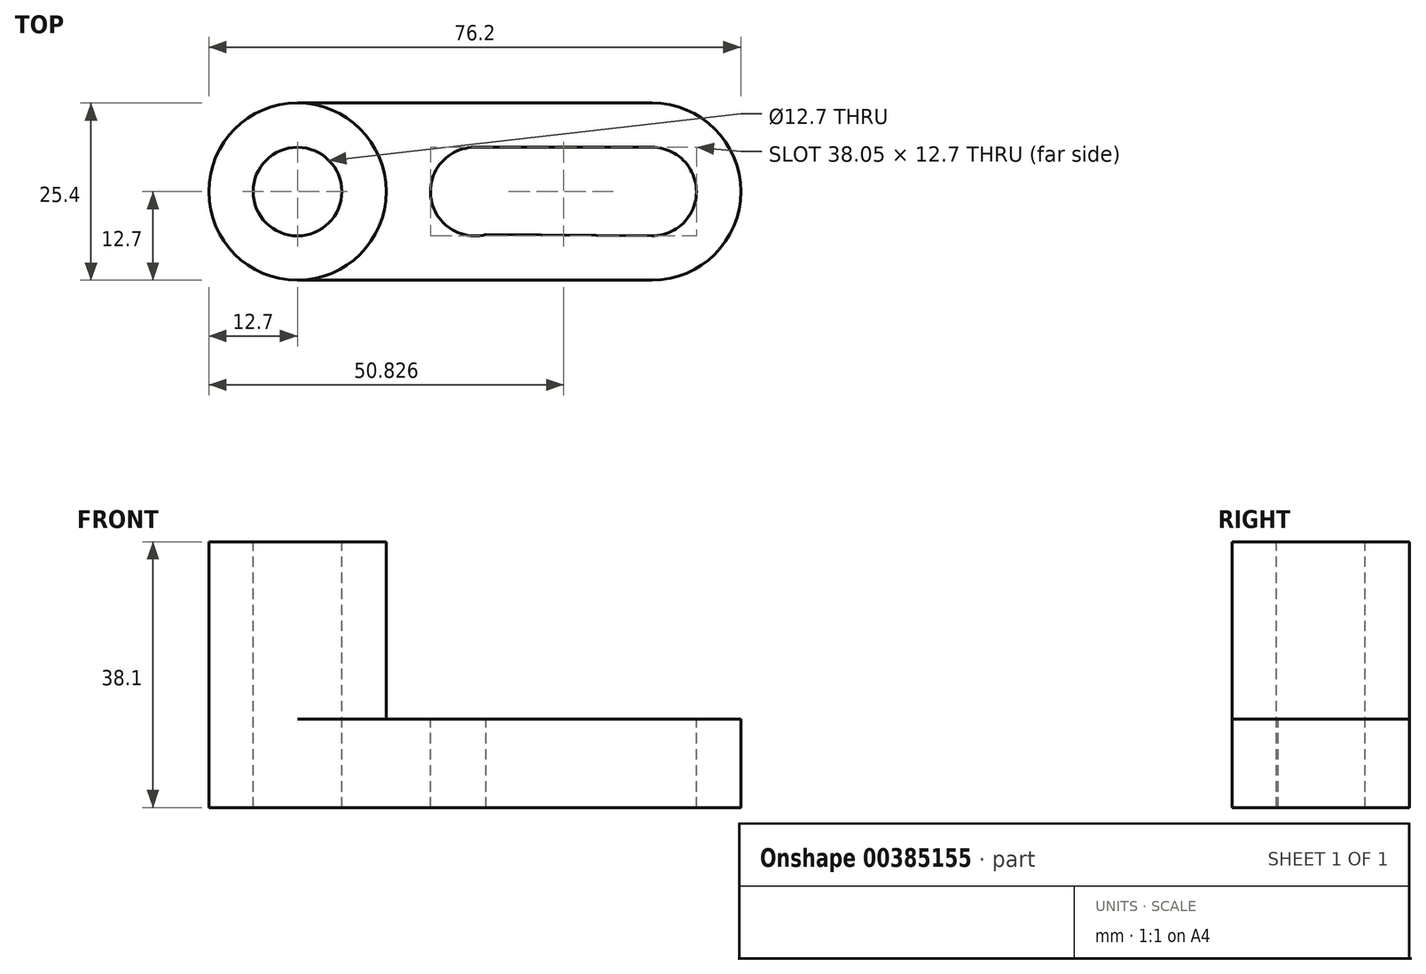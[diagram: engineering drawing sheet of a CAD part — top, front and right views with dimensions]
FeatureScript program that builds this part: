
annotation { "Feature Type Name" : "Feature", "Feature Type Description" : "" }
export const myFeature = defineFeature(function(context is Context, id is Id, definition is map)
    precondition{}
    {
        {
            var Q0;
            Q0=qCreatedBy(makeId("Front.planeOp"),FACE);
            var sketch = newSketch(context, id + "F0", { "sketchPlane" : qUnion([Q0])});
            skLineSegment(sketch, "E0", {"start": v(0, 0) * mm, "end": v(0, 38.1) * mm});
            skLineSegment(sketch, "E1", {"start": v(0, 38.1) * mm, "end": v(25.4, 38.1) * mm});
            skLineSegment(sketch, "E2", {"start": v(25.4, 38.1) * mm, "end": v(25.4, 12.7) * mm});
            skLineSegment(sketch, "E3", {"start": v(25.4, 12.7) * mm, "end": v(76.2, 12.7) * mm});
            skLineSegment(sketch, "E4", {"start": v(76.2, 12.7) * mm, "end": v(76.2, 0) * mm});
            skLineSegment(sketch, "E5", {"start": v(76.2, 0) * mm, "end": v(0, 0) * mm});
            skSolve(sketch);
        }
        {
            var Q0;
            Q0 = qSketchRegion(id + "F0", true);
            extrude(context, id + "F1", {"entities" : qUnion([Q0]), "depth" : 25.4 * mm});
        }
        {
            var Q0;
            Q0=makeQuery(id+"F1.opExtrude","SWEPT_FACE",FACE,{"disambiguationData":[OSD([sQuery(id+"F0.wireOp",EDGE,"E3")])]});
            var sketch = newSketch(context, id + "F2", { "sketchPlane" : qUnion([Q0])});
            skCircle(sketch, "E6", {"center": v(38.1, -12.7) * mm, "radius": 6.35 * mm});
            skCircle(sketch, "E7", {"center": v(63.5, -12.7) * mm, "radius": 6.35 * mm});
            skLineSegment(sketch, "E8", {"start": v(38.1, -6.35) * mm, "end": v(63.5, -6.35) * mm});
            skLineSegment(sketch, "E9", {"start": v(39.7, -18.84) * mm, "end": v(63.44, -19.05) * mm});
            skSolve(sketch);
        }
        {
            var Q0;
            {var subQ0=sQuery(id+"F2.wireOp",EDGE,"E6");var subQ1=makeQuery(id+"F2.imprint","INTERSECT",VERTEX,{"derivedFrom":[subQ0,sQuery(id+"F2.wireOp",EDGE,"E8")]});Q0=makeQuery(id+"F2.imprint","IMPRINT",FACE,{"disambiguationData":[TD([[makeQuery(id+"F2.imprint","IMPRINT",EDGE,{"disambiguationData":[TD([[subQ1,-1.0]])],"derivedFrom":subQ0}),1.0]])]});}
            var Q1;
            {var subQ0=sQuery(id+"F2.wireOp",EDGE,"E8");Q1=makeQuery(id+"F2.imprint","IMPRINT",FACE,{"disambiguationData":[TD([[makeQuery(id+"F2.imprint","IMPRINT",EDGE,{"derivedFrom":subQ0}),-1.0]])]});}
            var Q2;
            {var subQ0=sQuery(id+"F2.wireOp",EDGE,"E7");var subQ1=makeQuery(id+"F2.imprint","INTERSECT",VERTEX,{"derivedFrom":[subQ0,sQuery(id+"F2.wireOp",EDGE,"E8")]});Q2=makeQuery(id+"F2.imprint","IMPRINT",FACE,{"disambiguationData":[TD([[makeQuery(id+"F2.imprint","IMPRINT",EDGE,{"disambiguationData":[TD([[subQ1,-1.0]])],"derivedFrom":subQ0}),1.0]])]});}
            extrude(context, id + "F3", {"entities" : qUnion([Q0, Q1, Q2]), "operationType" : NewBodyOperationType.REMOVE, "oppositeDirection" : true, "depth" : 25.4 * mm});
        }
        {
            var Q0;
            Q0=makeQuery(id+"F1.opExtrude","SWEPT_FACE",FACE,{"disambiguationData":[OSD([sQuery(id+"F0.wireOp",EDGE,"E1")])]});
            var sketch = newSketch(context, id + "F4", { "sketchPlane" : qUnion([Q0])});
            skCircle(sketch, "E10", {"center": v(12.7, -12.7) * mm, "radius": 12.7 * mm});
            skPoint(sketch, "E10.centerSnap0", {"position": v(25.4, -12.7) * mm});
            skSolve(sketch);
        }
        {
            var Q0;
            {var subQ0=sQuery(id+"F4.wireOp",EDGE,"E10");var subQ1=sQuery(id+"F0.wireOp",EDGE,"E1");var subQ2=makeQuery(id+"F1.opExtrude","CAP_EDGE",EDGE,{"disambiguationData":[OSD([subQ1])],"isStart":true});var subQ3=makeQuery(id+"F4.imprint","INTERSECT",VERTEX,{"derivedFrom":[subQ2,subQ0]});Q0=makeQuery(id+"F4.imprint","IMPRINT",FACE,{"disambiguationData":[TD([[makeQuery(id+"F4.imprint","IMPRINT",EDGE,{"disambiguationData":[TD([[subQ3,1.0]])],"derivedFrom":subQ0}),-1.0]])]});}
            var Q1;
            {var subQ0=sQuery(id+"F4.wireOp",EDGE,"E10");var subQ1=sQuery(id+"F0.wireOp",EDGE,"E1");var subQ2=makeQuery(id+"F1.opExtrude","CAP_EDGE",EDGE,{"disambiguationData":[OSD([subQ1])],"isStart":true});var subQ3=makeQuery(id+"F4.imprint","INTERSECT",VERTEX,{"derivedFrom":[subQ2,subQ0]});Q1=makeQuery(id+"F4.imprint","IMPRINT",FACE,{"disambiguationData":[TD([[makeQuery(id+"F4.imprint","IMPRINT",EDGE,{"disambiguationData":[TD([[subQ3,-1.0]])],"derivedFrom":subQ0}),-1.0]])]});}
            var Q2;
            {var subQ0=sQuery(id+"F4.wireOp",EDGE,"E10");var subQ1=sQuery(id+"F0.wireOp",EDGE,"E1");var subQ4=makeQuery(id+"F1.opExtrude","CAP_EDGE",EDGE,{"disambiguationData":[OSD([subQ1])],"isStart":false});var subQ5=makeQuery(id+"F4.imprint","INTERSECT",VERTEX,{"derivedFrom":[subQ4,subQ0]});Q2=makeQuery(id+"F4.imprint","IMPRINT",FACE,{"disambiguationData":[TD([[makeQuery(id+"F4.imprint","IMPRINT",EDGE,{"disambiguationData":[TD([[subQ5,1.0]])],"derivedFrom":subQ0}),-1.0]])]});}
            var Q3;
            {var subQ0=sQuery(id+"F4.wireOp",EDGE,"E10");var subQ1=sQuery(id+"F0.wireOp",EDGE,"E1");var subQ4=makeQuery(id+"F1.opExtrude","CAP_EDGE",EDGE,{"disambiguationData":[OSD([subQ1])],"isStart":false});var subQ5=makeQuery(id+"F4.imprint","INTERSECT",VERTEX,{"derivedFrom":[subQ4,subQ0]});Q3=makeQuery(id+"F4.imprint","IMPRINT",FACE,{"disambiguationData":[TD([[makeQuery(id+"F4.imprint","IMPRINT",EDGE,{"disambiguationData":[TD([[subQ5,-1.0]])],"derivedFrom":subQ0}),-1.0]])]});}
            extrude(context, id + "F5", {"entities" : qUnion([Q0, Q1, Q2, Q3]), "operationType" : NewBodyOperationType.REMOVE, "oppositeDirection" : true, "depth" : 25.4 * mm});
        }
        {
            var Q0;
            {var subQ0=sQuery(id+"F0.wireOp",EDGE,"E1");var subQ1=makeQuery(id+"F1.opExtrude","CAP_EDGE",EDGE,{"disambiguationData":[OSD([subQ0])],"isStart":true});var subQ2=sQuery(id+"F0.wireOp",EDGE,"E0");var subQ3=makeQuery(id+"F1.opExtrude","SWEPT_EDGE",EDGE,{"disambiguationData":[OSD([subQ2,subQ0])]});var subQ4=makeQuery(id+"F4.imprint","INTERSECT",VERTEX,{"derivedFrom":[subQ3,subQ1]});var subQ5=sQuery(id+"F4.wireOp",EDGE,"E10");var subQ6=makeQuery(id+"F4.imprint","INTERSECT",VERTEX,{"derivedFrom":[subQ1,subQ5]});Q0=makeQuery(id+"F5.boolean.opBoolean","COPY",FACE,{"derivedFrom":makeQuery(id+"F5.opExtrude","CAP_FACE",FACE,{"disambiguationData":[OSD([subQ2,subQ0,subQ5]),TDD([makeQuery(id+"F4.imprint","IMPRINT",EDGE,{"disambiguationData":[TD([[subQ6,-1.0]])],"derivedFrom":subQ5}),makeQuery(id+"F4.imprint","IMPRINT",EDGE,{"disambiguationData":[TD([[subQ4,1.0]])],"derivedFrom":subQ3}),makeQuery(id+"F4.imprint","IMPRINT",EDGE,{"disambiguationData":[TD([[subQ6,1.0]])],"derivedFrom":subQ1})])],"isStart":false})});}
            var Q1;
            {var subQ0=sQuery(id+"F0.wireOp",EDGE,"E1");var subQ1=makeQuery(id+"F1.opExtrude","CAP_EDGE",EDGE,{"disambiguationData":[OSD([subQ0])],"isStart":false});var subQ2=sQuery(id+"F0.wireOp",EDGE,"E0");var subQ3=makeQuery(id+"F1.opExtrude","SWEPT_EDGE",EDGE,{"disambiguationData":[OSD([subQ2,subQ0])]});var subQ4=makeQuery(id+"F4.imprint","INTERSECT",VERTEX,{"derivedFrom":[subQ3,subQ1]});var subQ5=sQuery(id+"F4.wireOp",EDGE,"E10");var subQ6=makeQuery(id+"F4.imprint","INTERSECT",VERTEX,{"derivedFrom":[subQ1,subQ5]});Q1=makeQuery(id+"F5.boolean.opBoolean","COPY",FACE,{"derivedFrom":makeQuery(id+"F5.opExtrude","CAP_FACE",FACE,{"disambiguationData":[OSD([subQ2,subQ0,subQ5]),TDD([makeQuery(id+"F4.imprint","IMPRINT",EDGE,{"disambiguationData":[TD([[subQ6,1.0]])],"derivedFrom":subQ5}),makeQuery(id+"F4.imprint","IMPRINT",EDGE,{"disambiguationData":[TD([[subQ4,-1.0]])],"derivedFrom":subQ3}),makeQuery(id+"F4.imprint","IMPRINT",EDGE,{"disambiguationData":[TD([[subQ6,1.0]])],"derivedFrom":subQ1})])],"isStart":false})});}
            extrude(context, id + "F6", {"entities" : qUnion([Q0, Q1]), "operationType" : NewBodyOperationType.REMOVE, "oppositeDirection" : true, "depth" : 25.4 * mm});
        }
        {
            var Q0;
            Q0=makeQuery(id+"F1.opExtrude","SWEPT_FACE",FACE,{"disambiguationData":[OSD([sQuery(id+"F0.wireOp",EDGE,"E1")])]});
            var sketch = newSketch(context, id + "F7", { "sketchPlane" : qUnion([Q0])});
            skCircle(sketch, "E11", {"center": v(12.7, -12.7) * mm, "radius": 6.35 * mm});
            skSolve(sketch);
        }
        {
            var Q0;
            Q0=makeQuery(id+"F7.imprint","IMPRINT",FACE,{"disambiguationData":[TD([[makeQuery(id+"F7.imprint","IMPRINT",EDGE,{"derivedFrom":sQuery(id+"F7.wireOp",EDGE,"E11")}),1.0]])]});
            extrude(context, id + "F8", {"entities" : qUnion([Q0]), "operationType" : NewBodyOperationType.REMOVE, "oppositeDirection" : true, "depth" : 38.1 * mm});
        }
        {
            var Q0;
            {var subQ0=sQuery(id+"F0.wireOp",EDGE,"E1");var subQ1=makeQuery(id+"F1.opExtrude","CAP_EDGE",EDGE,{"disambiguationData":[OSD([subQ0])],"isStart":false});var subQ2=sQuery(id+"F0.wireOp",EDGE,"E2");var subQ3=makeQuery(id+"F1.opExtrude","SWEPT_EDGE",EDGE,{"disambiguationData":[OSD([subQ0,subQ2])]});var subQ4=makeQuery(id+"F4.imprint","INTERSECT",VERTEX,{"derivedFrom":[subQ3,subQ1]});var subQ5=sQuery(id+"F4.wireOp",EDGE,"E10");var subQ6=makeQuery(id+"F4.imprint","INTERSECT",VERTEX,{"derivedFrom":[subQ1,subQ5]});var subQ8=makeQuery(id+"F1.opExtrude","CAP_EDGE",EDGE,{"disambiguationData":[OSD([subQ0])],"isStart":true});var subQ9=makeQuery(id+"F4.imprint","INTERSECT",VERTEX,{"derivedFrom":[subQ3,subQ8]});var subQ10=makeQuery(id+"F4.imprint","INTERSECT",VERTEX,{"derivedFrom":[subQ8,subQ5]});Q0=makeQuery(id+"F5.boolean.opBoolean","MERGE",FACE,{"derivedFrom":[makeQuery(id+"F1.opExtrude","SWEPT_FACE",FACE,{"disambiguationData":[OSD([sQuery(id+"F0.wireOp",EDGE,"E3")])]}),makeQuery(id+"F5.opExtrude","CAP_FACE",FACE,{"disambiguationData":[OSD([subQ0,subQ2,subQ5]),TDD([makeQuery(id+"F4.imprint","IMPRINT",EDGE,{"disambiguationData":[TD([[subQ10,1.0]])],"derivedFrom":subQ5}),makeQuery(id+"F4.imprint","IMPRINT",EDGE,{"disambiguationData":[TD([[subQ9,1.0]])],"derivedFrom":subQ3}),makeQuery(id+"F4.imprint","IMPRINT",EDGE,{"disambiguationData":[TD([[subQ10,-1.0]])],"derivedFrom":subQ8})])],"isStart":false}),makeQuery(id+"F5.opExtrude","CAP_FACE",FACE,{"disambiguationData":[OSD([subQ0,subQ2,subQ5]),TDD([makeQuery(id+"F4.imprint","IMPRINT",EDGE,{"disambiguationData":[TD([[subQ6,-1.0]])],"derivedFrom":subQ5}),makeQuery(id+"F4.imprint","IMPRINT",EDGE,{"disambiguationData":[TD([[subQ4,-1.0]])],"derivedFrom":subQ3}),makeQuery(id+"F4.imprint","IMPRINT",EDGE,{"disambiguationData":[TD([[subQ6,-1.0]])],"derivedFrom":subQ1})])],"isStart":false})]});}
            var sketch = newSketch(context, id + "F9", { "sketchPlane" : qUnion([Q0])});
            skArc(sketch, "E12", {"start": v(63.5, -25.4) * mm, "mid": v(76.2, -12.7) * mm, "end": v(63.5, 0) * mm});
            skSolve(sketch);
        }
        {
            var Q0;
            {var subQ0=sQuery(id+"F9.wireOp",EDGE,"E12");var subQ3=sQuery(id+"F0.wireOp",EDGE,"E3");var subQ6=makeQuery(id+"F1.opExtrude","SWEPT_EDGE",EDGE,{"disambiguationData":[OSD([subQ3,sQuery(id+"F0.wireOp",EDGE,"E4")])]});var subQ7=makeQuery(id+"F9.imprint","INTERSECT",VERTEX,{"derivedFrom":[subQ6,subQ0]});Q0=makeQuery(id+"F9.imprint","IMPRINT",FACE,{"disambiguationData":[TD([[makeQuery(id+"F9.imprint","IMPRINT",EDGE,{"disambiguationData":[TD([[subQ7,1.0]])],"derivedFrom":subQ0}),-1.0]])]});}
            var Q1;
            {var subQ0=sQuery(id+"F9.wireOp",EDGE,"E12");var subQ3=sQuery(id+"F0.wireOp",EDGE,"E3");var subQ6=makeQuery(id+"F1.opExtrude","SWEPT_EDGE",EDGE,{"disambiguationData":[OSD([subQ3,sQuery(id+"F0.wireOp",EDGE,"E4")])]});var subQ7=makeQuery(id+"F9.imprint","INTERSECT",VERTEX,{"derivedFrom":[subQ6,subQ0]});Q1=makeQuery(id+"F9.imprint","IMPRINT",FACE,{"disambiguationData":[TD([[makeQuery(id+"F9.imprint","IMPRINT",EDGE,{"disambiguationData":[TD([[subQ7,-1.0]])],"derivedFrom":subQ0}),-1.0]])]});}
            extrude(context, id + "F10", {"entities" : qUnion([Q0, Q1]), "operationType" : NewBodyOperationType.REMOVE, "oppositeDirection" : true, "depth" : 25.4 * mm});
        }
    });
